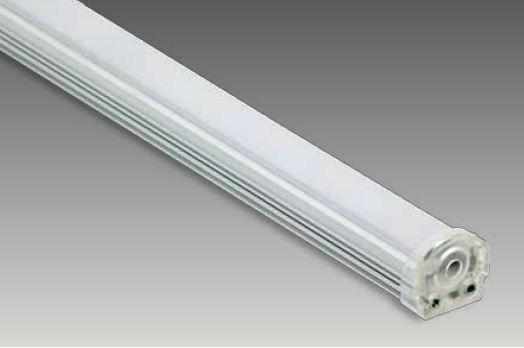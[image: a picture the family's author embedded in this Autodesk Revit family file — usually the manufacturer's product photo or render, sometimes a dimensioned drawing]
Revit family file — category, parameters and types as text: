
# Revit family: SD 1000 CVI
name_source: partatom
category: Lighting Fixtures
revit_build: Autodesk Revit 2017 (Build: 20160225_1515(x64)
units: mm (PartAtom-declared; Revit-internal decimal feet)

## family parameters
Cut with Voids When Loaded = No
Host = Face
Light Source = Yes
Part Type = Normal
Room Calculation Point = No
Round Connector Dimension = Use Diameter
Shared = No

## types (2) — shared parameters
Apparent Load = 16 VA
Color Filter = 16777215
Default Elevation = 1219 mm
Dimming Lamp Color Temperature Shift = <None>
Emit Shape Visible in Rendering = Yes
Emit from Rectangle Length = 995 mm  [stored 3.26444 ft]
Emit from Rectangle Width = 15 mm  [stored 0.0492126 ft]
Light Source Symbol Size = 610 mm
Manufacturer = ARLIGHT
Type Image = SD 1000 CVI.JPG
Wattage Comments = 16

## type names (no varying parameters)
- SDCVI.1000.16.30
- SDCVI.1000.16.40

note: [stored X ft] marks values corroborated as IEEE doubles in the binary element streams (Revit-internal decimal feet)

## geometry (parser evidence)
native form markers: Sweep x2
no freeform markers — native parametric forms only
